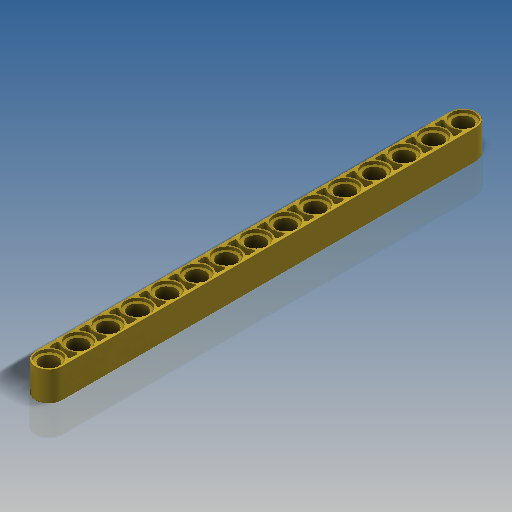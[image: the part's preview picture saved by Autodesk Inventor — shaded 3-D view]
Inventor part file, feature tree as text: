
AUTODESK INVENTOR PART (.ipt)
format: ipt  version: 2018.3 (Build 223284000, 284)  size: 610,816 bytes
history: native  units: mm
features: extrude x3, sketch x2, projected_geometry x2, mirror x1, fillet x1
ambient origin geometry x8: Origin, YZ Plane, XZ Plane, XY Plane, X Axis, Y Axis, Z Axis, Center Point
bodies: Solid1 (feature_tree)
feature tree (9):
  extrude  "Extrusion1"  Depth=7.2mm
  sketch  "Sketch6"  dims[d41=0.8mm d42=0.0mm d43=3.1mm d44=0.0mm d48=112.0mm d49=6.4mm d50=4.8mm d51=8.0mm d52=0.8mm d53=140.0mm d55=8.0mm d56=10.0mm d58=10.0mm d60=0.4mm d61=0.1mm]
  extrude  "Extrusion7"  Depth=3.1mm TaperAngle=0.0deg
  extrude  "Extrusion8"  Depth=0.1mm
  mirror  "Mirror1"
  fillet  "Fillet2"  Radius=6.4mm
  sketch  "Sketch1"  dims[d14=8.0mm d15=0.0mm d32=7.2mm]
  projected_geometry  "Projected Loop3"
  projected_geometry  "Projected Loop4"
